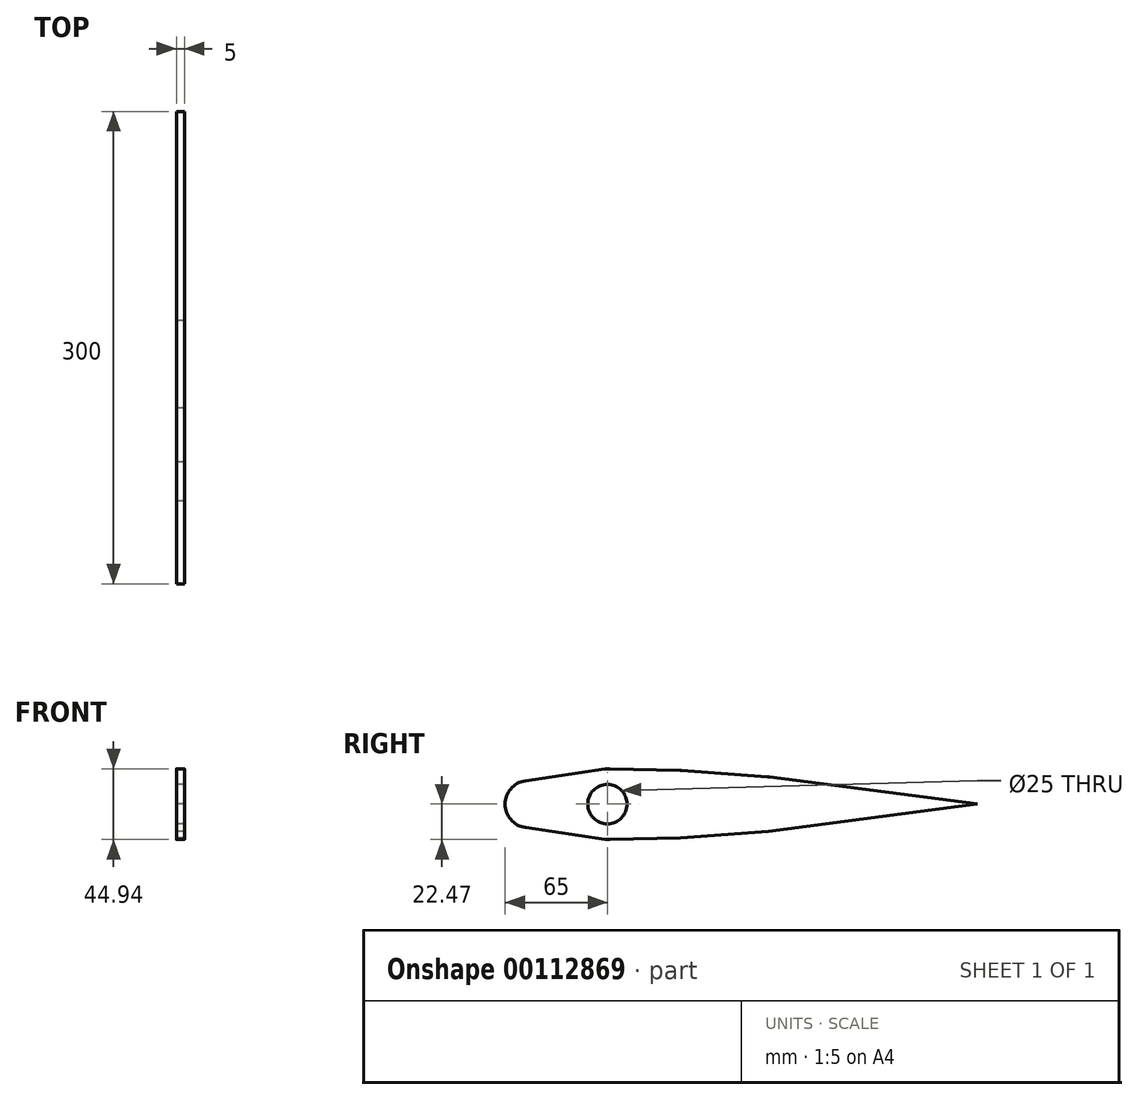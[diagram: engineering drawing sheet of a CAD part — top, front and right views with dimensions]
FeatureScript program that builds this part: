
annotation { "Feature Type Name" : "Feature", "Feature Type Description" : "" }
export const myFeature = defineFeature(function(context is Context, id is Id, definition is map)
    precondition{}
    {
        {
            var Q0;
            Q0=qCreatedBy(makeId("Right.planeOp"),FACE);
            var sketch = newSketch(context, id + "F0", { "sketchPlane" : qUnion([Q0])});
            skCircle(sketch, "E0", {"center": v(0, 0) * mm, "radius": 12.5 * mm});
            skLineSegment(sketch, "E1", {"start": v(-65, 0) * mm, "end": v(235, 0) * mm, "construction": true});
            skCircle(sketch, "E2", {"center": v(0, 0) * mm, "radius": 22.5 * mm, "construction": true});
            skCircle(sketch, "E3", {"center": v(-50, 0) * mm, "radius": 15 * mm, "construction": true});
            skCircle(sketch, "E4", {"center": v(100, 0) * mm, "radius": 17.5 * mm, "construction": true});
            skLineSegment(sketch, "E5", {"start": v(235, 0) * mm, "end": v(102.27, 17.35) * mm});
            skLineSegment(sketch, "E6", {"start": v(235, 0) * mm, "end": v(102.27, -17.35) * mm});
            skLineSegment(sketch, "E7", {"start": v(0, -22.5) * mm, "end": v(-52.18, -14.84) * mm});
            skLineSegment(sketch, "E8", {"start": v(0, 22.5) * mm, "end": v(-52.18, 14.84) * mm});
            skArc(sketch, "E9", {"start": v(-52.18, 14.84) * mm, "mid": v(-65, 0) * mm, "end": v(-52.18, -14.84) * mm});
            skCircle(sketch, "E10", {"center": v(44.9, 0) * mm, "radius": 21.5 * mm, "construction": true});
            skLineSegment(sketch, "E11", {"start": v(102.27, 17.35) * mm, "end": v(46.48, 21.44) * mm});
            skLineSegment(sketch, "E12", {"start": v(46.48, 21.44) * mm, "end": v(0, 22.5) * mm});
            skLineSegment(sketch, "E13", {"start": v(102.27, -17.35) * mm, "end": v(46.48, -21.44) * mm});
            skLineSegment(sketch, "E14", {"start": v(46.48, -21.44) * mm, "end": v(0, -22.5) * mm});
            skSolve(sketch);
        }
        {
            var Q0;
            Q0 = qSketchRegion(id + "F0", true);
            extrude(context, id + "F1", {"entities" : qUnion([Q0]), "endBound" : BoundingType.SYMMETRIC, "depth" : 5 * mm});
        }
        {
            var Q0;
            Q0=makeQuery(id+"F1.opExtrude","SWEPT_EDGE",EDGE,{"disambiguationData":[OSD([sQuery(id+"F0.wireOp",EDGE,"E8"),sQuery(id+"F0.wireOp",EDGE,"E12")])]});
            var Q1;
            Q1=makeQuery(id+"F1.opExtrude","SWEPT_EDGE",EDGE,{"disambiguationData":[OSD([sQuery(id+"F0.wireOp",EDGE,"E7"),sQuery(id+"F0.wireOp",EDGE,"E14")])]});
            var Q2;
            Q2=makeQuery(id+"F1.opExtrude","SWEPT_EDGE",EDGE,{"disambiguationData":[OSD([sQuery(id+"F0.wireOp",EDGE,"E11"),sQuery(id+"F0.wireOp",EDGE,"E12")])]});
            var Q3;
            Q3=makeQuery(id+"F1.opExtrude","SWEPT_EDGE",EDGE,{"disambiguationData":[OSD([sQuery(id+"F0.wireOp",EDGE,"E5"),sQuery(id+"F0.wireOp",EDGE,"E11")])]});
            fillet(context, id + "F2", {"entities" : qUnion([Q0, Q1, Q2, Q3]), "radius" : 20 * mm, "tangentPropagation" : true, "allowEdgeOverflow" : false});
        }
    });
